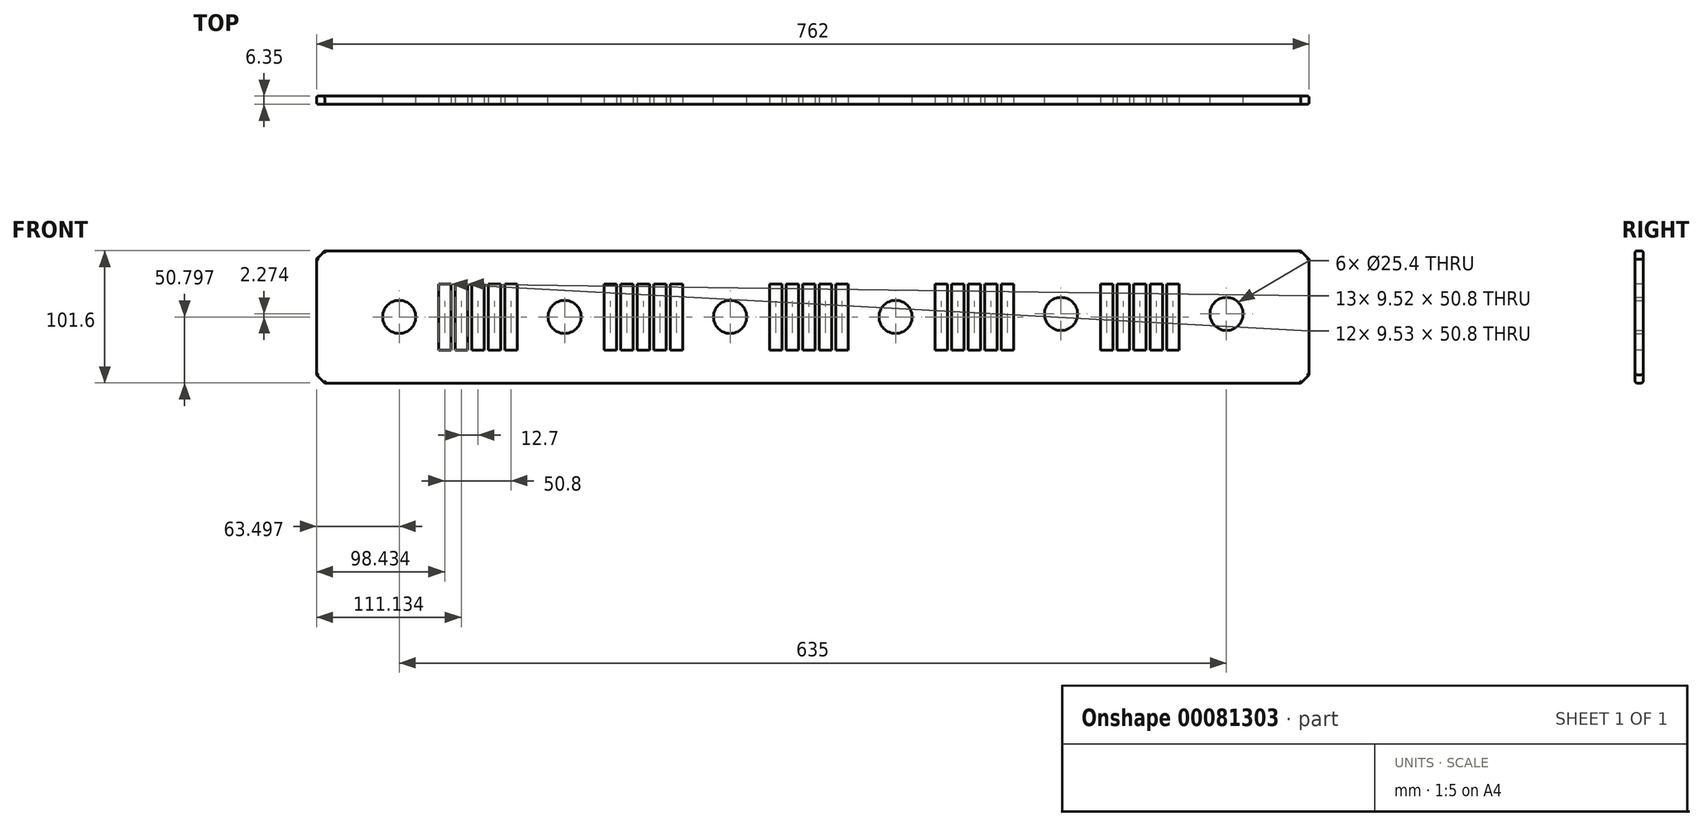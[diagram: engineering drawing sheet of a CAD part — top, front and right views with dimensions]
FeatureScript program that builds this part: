
annotation { "Feature Type Name" : "Feature", "Feature Type Description" : "" }
export const myFeature = defineFeature(function(context is Context, id is Id, definition is map)
    precondition{}
    {
        {
            var Q0;
            Q0=qCreatedBy(makeId("Front.planeOp"),FACE);
            var sketch = newSketch(context, id + "F0", { "sketchPlane" : qUnion([Q0])});
            skLineSegment(sketch, "E0.bottom", {"start": v(-162.42, 48.72) * mm, "end": v(599.58, 48.72) * mm});
            skLineSegment(sketch, "E0.top", {"start": v(-162.42, -52.88) * mm, "end": v(599.58, -52.88) * mm});
            skLineSegment(sketch, "E0.left", {"start": v(-162.42, 48.72) * mm, "end": v(-162.42, -52.88) * mm});
            skLineSegment(sketch, "E0.right", {"start": v(599.58, 48.72) * mm, "end": v(599.58, -52.88) * mm});
            skPoint(sketch, "E1.centerSnap0", {"position": v(-162.42, -2.08) * mm});
            skCircle(sketch, "E2", {"center": v(-98.92, -2.08) * mm, "radius": 12.7 * mm});
            skCircle(sketch, "E3", {"center": v(28.08, -2.08) * mm, "radius": 12.7 * mm});
            skCircle(sketch, "E4", {"center": v(155.08, -2.08) * mm, "radius": 12.7 * mm});
            skCircle(sketch, "E5", {"center": v(282.08, -2.08) * mm, "radius": 12.7 * mm});
            skCircle(sketch, "E6", {"center": v(409.08, 0.2) * mm, "radius": 12.7 * mm});
            skCircle(sketch, "E7", {"center": v(536.08, 0.2) * mm, "radius": 12.7 * mm});
            skSolve(sketch);
        }
        {
            var Q0;
            Q0=makeQuery(id+"F0.imprint","IMPRINT",FACE,{"disambiguationData":[TD([[makeQuery(id+"F0.imprint","IMPRINT",EDGE,{"derivedFrom":sQuery(id+"F0.wireOp",EDGE,"E0.bottom")}),-1.0]])]});
            var sketch = newSketch(context, id + "F1", { "sketchPlane" : qUnion([Q0])});
            skSolve(sketch);
        }
        {
            var Q0;
            Q0 = qSketchRegion(id + "F1", true);
            var Q1;
            Q1=makeQuery(id+"F0.imprint","IMPRINT",FACE,{"disambiguationData":[TD([[makeQuery(id+"F0.imprint","IMPRINT",EDGE,{"derivedFrom":sQuery(id+"F0.wireOp",EDGE,"E0.bottom")}),-1.0]])]});
            extrude(context, id + "F2", {"entities" : qUnion([Q0, Q1]), "depth" : 6.35 * mm});
        }
        {
            var Q0;
            Q0=makeQuery(id+"F2.opExtrude","SWEPT_EDGE",EDGE,{"disambiguationData":[OSD([sQuery(id+"F0.wireOp",EDGE,"E0.bottom"),sQuery(id+"F0.wireOp",EDGE,"E0.left")])]});
            var Q1;
            Q1=makeQuery(id+"F2.opExtrude","SWEPT_EDGE",EDGE,{"disambiguationData":[OSD([sQuery(id+"F0.wireOp",EDGE,"E0.top"),sQuery(id+"F0.wireOp",EDGE,"E0.left")])]});
            var Q2;
            Q2=makeQuery(id+"F2.opExtrude","SWEPT_EDGE",EDGE,{"disambiguationData":[OSD([sQuery(id+"F0.wireOp",EDGE,"E0.top"),sQuery(id+"F0.wireOp",EDGE,"E0.right")])]});
            var Q3;
            Q3=makeQuery(id+"F2.opExtrude","SWEPT_EDGE",EDGE,{"disambiguationData":[OSD([sQuery(id+"F0.wireOp",EDGE,"E0.bottom"),sQuery(id+"F0.wireOp",EDGE,"E0.right")])]});
            chamfer(context, id + "F3", {"entities" : qUnion([Q0, Q1, Q2, Q3]), "width" : 6.35 * mm, "tangentPropagation" : true});
        }
        {
            var Q0;
            Q0=makeQuery(id+"F2.opExtrude","CAP_FACE",FACE,{"disambiguationData":[OSD([sQuery(id+"F0.wireOp",EDGE,"E0.bottom"),sQuery(id+"F0.wireOp",EDGE,"E0.top"),sQuery(id+"F0.wireOp",EDGE,"E0.left"),sQuery(id+"F0.wireOp",EDGE,"E0.right"),sQuery(id+"F0.wireOp",EDGE,"E2"),sQuery(id+"F0.wireOp",EDGE,"E3"),sQuery(id+"F0.wireOp",EDGE,"E4"),sQuery(id+"F0.wireOp",EDGE,"E5"),sQuery(id+"F0.wireOp",EDGE,"E6"),sQuery(id+"F0.wireOp",EDGE,"E7")])],"isStart":false});
            var sketch = newSketch(context, id + "F4", { "sketchPlane" : qUnion([Q0])});
            skLineSegment(sketch, "E8.bottom", {"start": v(-68.75, -27.48) * mm, "end": v(-59.22, -27.48) * mm});
            skLineSegment(sketch, "E8.top", {"start": v(-68.75, 23.32) * mm, "end": v(-59.22, 23.32) * mm});
            skLineSegment(sketch, "E8.left", {"start": v(-68.75, -27.48) * mm, "end": v(-68.75, 23.32) * mm});
            skLineSegment(sketch, "E8.right", {"start": v(-59.22, -27.48) * mm, "end": v(-59.22, 23.32) * mm});
            skLineSegment(sketch, "E9.1.0.0", {"start": v(-46.52, -27.48) * mm, "end": v(-46.52, 23.32) * mm});
            skLineSegment(sketch, "E9.1.0.1", {"start": v(-56.05, -27.48) * mm, "end": v(-46.52, -27.48) * mm});
            skLineSegment(sketch, "E9.1.0.2", {"start": v(-56.05, 23.32) * mm, "end": v(-46.52, 23.32) * mm});
            skLineSegment(sketch, "E9.1.0.3", {"start": v(-56.05, -27.48) * mm, "end": v(-56.05, 23.32) * mm});
            skLineSegment(sketch, "E9.2.0.0", {"start": v(-33.82, -27.48) * mm, "end": v(-33.82, 23.32) * mm});
            skLineSegment(sketch, "E9.2.0.1", {"start": v(-43.35, -27.48) * mm, "end": v(-33.82, -27.48) * mm});
            skLineSegment(sketch, "E9.2.0.2", {"start": v(-43.35, 23.32) * mm, "end": v(-33.82, 23.32) * mm});
            skLineSegment(sketch, "E9.2.0.3", {"start": v(-43.35, -27.48) * mm, "end": v(-43.35, 23.32) * mm});
            skLineSegment(sketch, "E9.3.0.0", {"start": v(-21.12, -27.48) * mm, "end": v(-21.12, 23.32) * mm});
            skLineSegment(sketch, "E9.3.0.1", {"start": v(-30.65, -27.48) * mm, "end": v(-21.12, -27.48) * mm});
            skLineSegment(sketch, "E9.3.0.2", {"start": v(-30.65, 23.32) * mm, "end": v(-21.12, 23.32) * mm});
            skLineSegment(sketch, "E9.3.0.3", {"start": v(-30.65, -27.48) * mm, "end": v(-30.65, 23.32) * mm});
            skLineSegment(sketch, "E9.4.0.0", {"start": v(-8.42, -27.48) * mm, "end": v(-8.42, 23.32) * mm});
            skLineSegment(sketch, "E9.4.0.1", {"start": v(-17.95, -27.48) * mm, "end": v(-8.42, -27.48) * mm});
            skLineSegment(sketch, "E9.4.0.2", {"start": v(-17.95, 23.32) * mm, "end": v(-8.42, 23.32) * mm});
            skLineSegment(sketch, "E9.4.0.3", {"start": v(-17.95, -27.48) * mm, "end": v(-17.95, 23.32) * mm});
            skLineSegment(sketch, "E9.direction1", {"start": v(-59.22, -27.48) * mm, "end": v(-46.52, -27.48) * mm, "construction": true});
            skLineSegment(sketch, "E10.bottom", {"start": v(58.25, -27.48) * mm, "end": v(67.78, -27.48) * mm});
            skLineSegment(sketch, "E10.top", {"start": v(58.25, 23.32) * mm, "end": v(67.78, 23.32) * mm});
            skLineSegment(sketch, "E10.left", {"start": v(58.25, -27.48) * mm, "end": v(58.25, 23.32) * mm});
            skLineSegment(sketch, "E10.right", {"start": v(67.78, -27.48) * mm, "end": v(67.78, 23.32) * mm});
            skLineSegment(sketch, "E11.1.0.0", {"start": v(80.48, -27.48) * mm, "end": v(80.48, 23.32) * mm});
            skLineSegment(sketch, "E11.1.0.1", {"start": v(70.95, -27.48) * mm, "end": v(80.48, -27.48) * mm});
            skLineSegment(sketch, "E11.1.0.2", {"start": v(70.95, 23.32) * mm, "end": v(80.48, 23.32) * mm});
            skLineSegment(sketch, "E11.1.0.3", {"start": v(70.95, -27.48) * mm, "end": v(70.95, 23.32) * mm});
            skLineSegment(sketch, "E11.2.0.0", {"start": v(93.18, -27.48) * mm, "end": v(93.18, 23.32) * mm});
            skLineSegment(sketch, "E11.2.0.1", {"start": v(83.65, -27.48) * mm, "end": v(93.18, -27.48) * mm});
            skLineSegment(sketch, "E11.2.0.2", {"start": v(83.65, 23.32) * mm, "end": v(93.18, 23.32) * mm});
            skLineSegment(sketch, "E11.2.0.3", {"start": v(83.65, -27.48) * mm, "end": v(83.65, 23.32) * mm});
            skLineSegment(sketch, "E11.3.0.0", {"start": v(105.88, -27.48) * mm, "end": v(105.88, 23.32) * mm});
            skLineSegment(sketch, "E11.3.0.1", {"start": v(96.35, -27.48) * mm, "end": v(105.88, -27.48) * mm});
            skLineSegment(sketch, "E11.3.0.2", {"start": v(96.35, 23.32) * mm, "end": v(105.88, 23.32) * mm});
            skLineSegment(sketch, "E11.3.0.3", {"start": v(96.35, -27.48) * mm, "end": v(96.35, 23.32) * mm});
            skLineSegment(sketch, "E11.4.0.0", {"start": v(118.58, -27.48) * mm, "end": v(118.58, 23.32) * mm});
            skLineSegment(sketch, "E11.4.0.1", {"start": v(109.05, -27.48) * mm, "end": v(118.58, -27.48) * mm});
            skLineSegment(sketch, "E11.4.0.2", {"start": v(109.05, 23.32) * mm, "end": v(118.58, 23.32) * mm});
            skLineSegment(sketch, "E11.4.0.3", {"start": v(109.05, -27.48) * mm, "end": v(109.05, 23.32) * mm});
            skLineSegment(sketch, "E11.direction1", {"start": v(67.78, -27.48) * mm, "end": v(80.48, -27.48) * mm, "construction": true});
            skLineSegment(sketch, "E12.bottom", {"start": v(185.25, -27.48) * mm, "end": v(194.78, -27.48) * mm});
            skLineSegment(sketch, "E12.top", {"start": v(185.25, 23.32) * mm, "end": v(194.78, 23.32) * mm});
            skLineSegment(sketch, "E12.left", {"start": v(185.25, -27.48) * mm, "end": v(185.25, 23.32) * mm});
            skLineSegment(sketch, "E12.right", {"start": v(194.78, -27.48) * mm, "end": v(194.78, 23.32) * mm});
            skLineSegment(sketch, "E13.1.0.0", {"start": v(207.48, -27.48) * mm, "end": v(207.48, 23.32) * mm});
            skLineSegment(sketch, "E13.1.0.1", {"start": v(197.95, -27.48) * mm, "end": v(207.48, -27.48) * mm});
            skLineSegment(sketch, "E13.1.0.2", {"start": v(197.95, 23.32) * mm, "end": v(207.48, 23.32) * mm});
            skLineSegment(sketch, "E13.1.0.3", {"start": v(197.95, -27.48) * mm, "end": v(197.95, 23.32) * mm});
            skLineSegment(sketch, "E13.2.0.0", {"start": v(220.18, -27.48) * mm, "end": v(220.18, 23.32) * mm});
            skLineSegment(sketch, "E13.2.0.1", {"start": v(210.65, -27.48) * mm, "end": v(220.18, -27.48) * mm});
            skLineSegment(sketch, "E13.2.0.2", {"start": v(210.65, 23.32) * mm, "end": v(220.18, 23.32) * mm});
            skLineSegment(sketch, "E13.2.0.3", {"start": v(210.65, -27.48) * mm, "end": v(210.65, 23.32) * mm});
            skLineSegment(sketch, "E13.3.0.0", {"start": v(232.88, -27.48) * mm, "end": v(232.88, 23.32) * mm});
            skLineSegment(sketch, "E13.3.0.1", {"start": v(223.35, -27.48) * mm, "end": v(232.88, -27.48) * mm});
            skLineSegment(sketch, "E13.3.0.2", {"start": v(223.35, 23.32) * mm, "end": v(232.88, 23.32) * mm});
            skLineSegment(sketch, "E13.3.0.3", {"start": v(223.35, -27.48) * mm, "end": v(223.35, 23.32) * mm});
            skLineSegment(sketch, "E13.4.0.0", {"start": v(245.58, -27.48) * mm, "end": v(245.58, 23.32) * mm});
            skLineSegment(sketch, "E13.4.0.1", {"start": v(236.05, -27.48) * mm, "end": v(245.58, -27.48) * mm});
            skLineSegment(sketch, "E13.4.0.2", {"start": v(236.05, 23.32) * mm, "end": v(245.58, 23.32) * mm});
            skLineSegment(sketch, "E13.4.0.3", {"start": v(236.05, -27.48) * mm, "end": v(236.05, 23.32) * mm});
            skLineSegment(sketch, "E13.direction1", {"start": v(194.78, -27.48) * mm, "end": v(207.48, -27.48) * mm, "construction": true});
            skLineSegment(sketch, "E14.bottom", {"start": v(312.25, -27.48) * mm, "end": v(321.78, -27.48) * mm});
            skLineSegment(sketch, "E14.top", {"start": v(312.25, 23.32) * mm, "end": v(321.78, 23.32) * mm});
            skLineSegment(sketch, "E14.left", {"start": v(312.25, -27.48) * mm, "end": v(312.25, 23.32) * mm});
            skLineSegment(sketch, "E14.right", {"start": v(321.78, -27.48) * mm, "end": v(321.78, 23.32) * mm});
            skLineSegment(sketch, "E15.1.0.0", {"start": v(334.48, -27.48) * mm, "end": v(334.48, 23.32) * mm});
            skLineSegment(sketch, "E15.1.0.1", {"start": v(324.95, -27.48) * mm, "end": v(334.48, -27.48) * mm});
            skLineSegment(sketch, "E15.1.0.2", {"start": v(324.95, 23.32) * mm, "end": v(334.48, 23.32) * mm});
            skLineSegment(sketch, "E15.1.0.3", {"start": v(324.95, -27.48) * mm, "end": v(324.95, 23.32) * mm});
            skLineSegment(sketch, "E15.2.0.0", {"start": v(347.18, -27.48) * mm, "end": v(347.18, 23.32) * mm});
            skLineSegment(sketch, "E15.2.0.1", {"start": v(337.65, -27.48) * mm, "end": v(347.18, -27.48) * mm});
            skLineSegment(sketch, "E15.2.0.2", {"start": v(337.65, 23.32) * mm, "end": v(347.18, 23.32) * mm});
            skLineSegment(sketch, "E15.2.0.3", {"start": v(337.65, -27.48) * mm, "end": v(337.65, 23.32) * mm});
            skLineSegment(sketch, "E15.3.0.0", {"start": v(359.88, -27.48) * mm, "end": v(359.88, 23.32) * mm});
            skLineSegment(sketch, "E15.3.0.1", {"start": v(350.35, -27.48) * mm, "end": v(359.88, -27.48) * mm});
            skLineSegment(sketch, "E15.3.0.2", {"start": v(350.35, 23.32) * mm, "end": v(359.88, 23.32) * mm});
            skLineSegment(sketch, "E15.3.0.3", {"start": v(350.35, -27.48) * mm, "end": v(350.35, 23.32) * mm});
            skLineSegment(sketch, "E15.4.0.0", {"start": v(372.58, -27.48) * mm, "end": v(372.58, 23.32) * mm});
            skLineSegment(sketch, "E15.4.0.1", {"start": v(363.05, -27.48) * mm, "end": v(372.58, -27.48) * mm});
            skLineSegment(sketch, "E15.4.0.2", {"start": v(363.05, 23.32) * mm, "end": v(372.58, 23.32) * mm});
            skLineSegment(sketch, "E15.4.0.3", {"start": v(363.05, -27.48) * mm, "end": v(363.05, 23.32) * mm});
            skLineSegment(sketch, "E15.direction1", {"start": v(321.78, -27.48) * mm, "end": v(334.48, -27.48) * mm, "construction": true});
            skLineSegment(sketch, "E16.bottom", {"start": v(439.25, -27.48) * mm, "end": v(448.78, -27.48) * mm});
            skLineSegment(sketch, "E16.top", {"start": v(439.25, 23.32) * mm, "end": v(448.78, 23.32) * mm});
            skLineSegment(sketch, "E16.left", {"start": v(439.25, -27.48) * mm, "end": v(439.25, 23.32) * mm});
            skLineSegment(sketch, "E16.right", {"start": v(448.78, -27.48) * mm, "end": v(448.78, 23.32) * mm});
            skLineSegment(sketch, "E17.1.0.0", {"start": v(461.48, -27.48) * mm, "end": v(461.48, 23.32) * mm});
            skLineSegment(sketch, "E17.1.0.1", {"start": v(451.95, -27.48) * mm, "end": v(461.48, -27.48) * mm});
            skLineSegment(sketch, "E17.1.0.2", {"start": v(451.95, 23.32) * mm, "end": v(461.48, 23.32) * mm});
            skLineSegment(sketch, "E17.1.0.3", {"start": v(451.95, -27.48) * mm, "end": v(451.95, 23.32) * mm});
            skLineSegment(sketch, "E17.2.0.0", {"start": v(474.18, -27.48) * mm, "end": v(474.18, 23.32) * mm});
            skLineSegment(sketch, "E17.2.0.1", {"start": v(464.65, -27.48) * mm, "end": v(474.18, -27.48) * mm});
            skLineSegment(sketch, "E17.2.0.2", {"start": v(464.65, 23.32) * mm, "end": v(474.18, 23.32) * mm});
            skLineSegment(sketch, "E17.2.0.3", {"start": v(464.65, -27.48) * mm, "end": v(464.65, 23.32) * mm});
            skLineSegment(sketch, "E17.3.0.0", {"start": v(486.88, -27.48) * mm, "end": v(486.88, 23.32) * mm});
            skLineSegment(sketch, "E17.3.0.1", {"start": v(477.35, -27.48) * mm, "end": v(486.88, -27.48) * mm});
            skLineSegment(sketch, "E17.3.0.2", {"start": v(477.35, 23.32) * mm, "end": v(486.88, 23.32) * mm});
            skLineSegment(sketch, "E17.3.0.3", {"start": v(477.35, -27.48) * mm, "end": v(477.35, 23.32) * mm});
            skLineSegment(sketch, "E17.4.0.0", {"start": v(499.58, -27.48) * mm, "end": v(499.58, 23.32) * mm});
            skLineSegment(sketch, "E17.4.0.1", {"start": v(490.05, -27.48) * mm, "end": v(499.58, -27.48) * mm});
            skLineSegment(sketch, "E17.4.0.2", {"start": v(490.05, 23.32) * mm, "end": v(499.58, 23.32) * mm});
            skLineSegment(sketch, "E17.4.0.3", {"start": v(490.05, -27.48) * mm, "end": v(490.05, 23.32) * mm});
            skLineSegment(sketch, "E17.direction1", {"start": v(448.78, -27.48) * mm, "end": v(461.48, -27.48) * mm, "construction": true});
            skSolve(sketch);
        }
        {
            var Q0;
            Q0 = qSketchRegion(id + "F4", true);
            extrude(context, id + "F5", {"entities" : qUnion([Q0]), "operationType" : NewBodyOperationType.REMOVE, "endBound" : BoundingType.THROUGH_ALL, "oppositeDirection" : true, "depth" : 25.4 * mm});
        }
        {
            var Q0;
            Q0=makeQuery(id+"F2.opExtrude","CAP_EDGE",EDGE,{"disambiguationData":[OSD([sQuery(id+"F0.wireOp",EDGE,"E0.bottom")])],"isStart":false});
            var Q1;
            Q1=makeQuery(id+"F2.opExtrude","CAP_EDGE",EDGE,{"disambiguationData":[OSD([sQuery(id+"F0.wireOp",EDGE,"E0.left")])],"isStart":true});
            var Q2;
            {var subQ0=sQuery(id+"F0.wireOp",EDGE,"E0.left");var subQ1=sQuery(id+"F0.wireOp",EDGE,"E0.bottom");Q2=makeQuery(id+"F3.opChamfer","BLEND_EDGE",EDGE,{"blendedFrom":[makeQuery(id+"F2.opExtrude","SWEPT_EDGE",EDGE,{"disambiguationData":[OSD([subQ1,subQ0])]}),makeQuery(id+"F2.opExtrude","CAP_FACE",FACE,{"disambiguationData":[OSD([subQ1,sQuery(id+"F0.wireOp",EDGE,"E0.top"),subQ0,sQuery(id+"F0.wireOp",EDGE,"E0.right"),sQuery(id+"F0.wireOp",EDGE,"E2"),sQuery(id+"F0.wireOp",EDGE,"E3"),sQuery(id+"F0.wireOp",EDGE,"E4"),sQuery(id+"F0.wireOp",EDGE,"E5"),sQuery(id+"F0.wireOp",EDGE,"E6"),sQuery(id+"F0.wireOp",EDGE,"E7")])],"isStart":false})],"blendedInto":[makeQuery(id+"F2.opExtrude","CAP_FACE",FACE,{"disambiguationData":[OSD([subQ1,sQuery(id+"F0.wireOp",EDGE,"E0.top"),subQ0,sQuery(id+"F0.wireOp",EDGE,"E0.right"),sQuery(id+"F0.wireOp",EDGE,"E2"),sQuery(id+"F0.wireOp",EDGE,"E3"),sQuery(id+"F0.wireOp",EDGE,"E4"),sQuery(id+"F0.wireOp",EDGE,"E5"),sQuery(id+"F0.wireOp",EDGE,"E6"),sQuery(id+"F0.wireOp",EDGE,"E7")])],"isStart":false})]});}
            var Q3;
            Q3=makeQuery(id+"F2.opExtrude","CAP_EDGE",EDGE,{"disambiguationData":[OSD([sQuery(id+"F0.wireOp",EDGE,"E0.left")])],"isStart":false});
            var Q4;
            {var subQ0=sQuery(id+"F0.wireOp",EDGE,"E0.left");var subQ1=sQuery(id+"F0.wireOp",EDGE,"E0.top");Q4=makeQuery(id+"F3.opChamfer","BLEND_EDGE",EDGE,{"blendedFrom":[makeQuery(id+"F2.opExtrude","SWEPT_EDGE",EDGE,{"disambiguationData":[OSD([subQ1,subQ0])]}),makeQuery(id+"F2.opExtrude","CAP_FACE",FACE,{"disambiguationData":[OSD([sQuery(id+"F0.wireOp",EDGE,"E0.bottom"),subQ1,subQ0,sQuery(id+"F0.wireOp",EDGE,"E0.right"),sQuery(id+"F0.wireOp",EDGE,"E2"),sQuery(id+"F0.wireOp",EDGE,"E3"),sQuery(id+"F0.wireOp",EDGE,"E4"),sQuery(id+"F0.wireOp",EDGE,"E5"),sQuery(id+"F0.wireOp",EDGE,"E6"),sQuery(id+"F0.wireOp",EDGE,"E7")])],"isStart":false})],"blendedInto":[makeQuery(id+"F2.opExtrude","CAP_FACE",FACE,{"disambiguationData":[OSD([sQuery(id+"F0.wireOp",EDGE,"E0.bottom"),subQ1,subQ0,sQuery(id+"F0.wireOp",EDGE,"E0.right"),sQuery(id+"F0.wireOp",EDGE,"E2"),sQuery(id+"F0.wireOp",EDGE,"E3"),sQuery(id+"F0.wireOp",EDGE,"E4"),sQuery(id+"F0.wireOp",EDGE,"E5"),sQuery(id+"F0.wireOp",EDGE,"E6"),sQuery(id+"F0.wireOp",EDGE,"E7")])],"isStart":false})]});}
            var Q5;
            Q5=makeQuery(id+"F2.opExtrude","CAP_EDGE",EDGE,{"disambiguationData":[OSD([sQuery(id+"F0.wireOp",EDGE,"E0.top")])],"isStart":false});
            var Q6;
            {var subQ0=sQuery(id+"F0.wireOp",EDGE,"E0.right");var subQ1=sQuery(id+"F0.wireOp",EDGE,"E0.top");Q6=makeQuery(id+"F3.opChamfer","BLEND_EDGE",EDGE,{"blendedFrom":[makeQuery(id+"F2.opExtrude","SWEPT_EDGE",EDGE,{"disambiguationData":[OSD([subQ1,subQ0])]}),makeQuery(id+"F2.opExtrude","CAP_FACE",FACE,{"disambiguationData":[OSD([sQuery(id+"F0.wireOp",EDGE,"E0.bottom"),subQ1,sQuery(id+"F0.wireOp",EDGE,"E0.left"),subQ0,sQuery(id+"F0.wireOp",EDGE,"E2"),sQuery(id+"F0.wireOp",EDGE,"E3"),sQuery(id+"F0.wireOp",EDGE,"E4"),sQuery(id+"F0.wireOp",EDGE,"E5"),sQuery(id+"F0.wireOp",EDGE,"E6"),sQuery(id+"F0.wireOp",EDGE,"E7")])],"isStart":false})],"blendedInto":[makeQuery(id+"F2.opExtrude","CAP_FACE",FACE,{"disambiguationData":[OSD([sQuery(id+"F0.wireOp",EDGE,"E0.bottom"),subQ1,sQuery(id+"F0.wireOp",EDGE,"E0.left"),subQ0,sQuery(id+"F0.wireOp",EDGE,"E2"),sQuery(id+"F0.wireOp",EDGE,"E3"),sQuery(id+"F0.wireOp",EDGE,"E4"),sQuery(id+"F0.wireOp",EDGE,"E5"),sQuery(id+"F0.wireOp",EDGE,"E6"),sQuery(id+"F0.wireOp",EDGE,"E7")])],"isStart":false})]});}
            var Q7;
            Q7=makeQuery(id+"F2.opExtrude","CAP_EDGE",EDGE,{"disambiguationData":[OSD([sQuery(id+"F0.wireOp",EDGE,"E0.right")])],"isStart":false});
            var Q8;
            {var subQ0=sQuery(id+"F0.wireOp",EDGE,"E0.right");var subQ1=sQuery(id+"F0.wireOp",EDGE,"E0.bottom");Q8=makeQuery(id+"F3.opChamfer","BLEND_EDGE",EDGE,{"blendedFrom":[makeQuery(id+"F2.opExtrude","SWEPT_EDGE",EDGE,{"disambiguationData":[OSD([subQ1,subQ0])]}),makeQuery(id+"F2.opExtrude","CAP_FACE",FACE,{"disambiguationData":[OSD([subQ1,sQuery(id+"F0.wireOp",EDGE,"E0.top"),sQuery(id+"F0.wireOp",EDGE,"E0.left"),subQ0,sQuery(id+"F0.wireOp",EDGE,"E2"),sQuery(id+"F0.wireOp",EDGE,"E3"),sQuery(id+"F0.wireOp",EDGE,"E4"),sQuery(id+"F0.wireOp",EDGE,"E5"),sQuery(id+"F0.wireOp",EDGE,"E6"),sQuery(id+"F0.wireOp",EDGE,"E7")])],"isStart":false})],"blendedInto":[makeQuery(id+"F2.opExtrude","CAP_FACE",FACE,{"disambiguationData":[OSD([subQ1,sQuery(id+"F0.wireOp",EDGE,"E0.top"),sQuery(id+"F0.wireOp",EDGE,"E0.left"),subQ0,sQuery(id+"F0.wireOp",EDGE,"E2"),sQuery(id+"F0.wireOp",EDGE,"E3"),sQuery(id+"F0.wireOp",EDGE,"E4"),sQuery(id+"F0.wireOp",EDGE,"E5"),sQuery(id+"F0.wireOp",EDGE,"E6"),sQuery(id+"F0.wireOp",EDGE,"E7")])],"isStart":false})]});}
            var Q9;
            {var subQ0=sQuery(id+"F0.wireOp",EDGE,"E0.right");var subQ1=sQuery(id+"F0.wireOp",EDGE,"E0.bottom");Q9=makeQuery(id+"F3.opChamfer","BLEND_EDGE",EDGE,{"blendedFrom":[makeQuery(id+"F2.opExtrude","SWEPT_EDGE",EDGE,{"disambiguationData":[OSD([subQ1,subQ0])]}),makeQuery(id+"F2.opExtrude","CAP_FACE",FACE,{"disambiguationData":[OSD([subQ1,sQuery(id+"F0.wireOp",EDGE,"E0.top"),sQuery(id+"F0.wireOp",EDGE,"E0.left"),subQ0,sQuery(id+"F0.wireOp",EDGE,"E2"),sQuery(id+"F0.wireOp",EDGE,"E3"),sQuery(id+"F0.wireOp",EDGE,"E4"),sQuery(id+"F0.wireOp",EDGE,"E5"),sQuery(id+"F0.wireOp",EDGE,"E6"),sQuery(id+"F0.wireOp",EDGE,"E7")])],"isStart":true})],"blendedInto":[makeQuery(id+"F2.opExtrude","CAP_FACE",FACE,{"disambiguationData":[OSD([subQ1,sQuery(id+"F0.wireOp",EDGE,"E0.top"),sQuery(id+"F0.wireOp",EDGE,"E0.left"),subQ0,sQuery(id+"F0.wireOp",EDGE,"E2"),sQuery(id+"F0.wireOp",EDGE,"E3"),sQuery(id+"F0.wireOp",EDGE,"E4"),sQuery(id+"F0.wireOp",EDGE,"E5"),sQuery(id+"F0.wireOp",EDGE,"E6"),sQuery(id+"F0.wireOp",EDGE,"E7")])],"isStart":true})]});}
            var Q10;
            Q10=makeQuery(id+"F2.opExtrude","CAP_EDGE",EDGE,{"disambiguationData":[OSD([sQuery(id+"F0.wireOp",EDGE,"E0.bottom")])],"isStart":true});
            var Q11;
            Q11=makeQuery(id+"F2.opExtrude","CAP_EDGE",EDGE,{"disambiguationData":[OSD([sQuery(id+"F0.wireOp",EDGE,"E0.right")])],"isStart":true});
            var Q12;
            {var subQ0=sQuery(id+"F0.wireOp",EDGE,"E0.right");var subQ1=sQuery(id+"F0.wireOp",EDGE,"E0.top");Q12=makeQuery(id+"F3.opChamfer","BLEND_EDGE",EDGE,{"blendedFrom":[makeQuery(id+"F2.opExtrude","SWEPT_EDGE",EDGE,{"disambiguationData":[OSD([subQ1,subQ0])]}),makeQuery(id+"F2.opExtrude","CAP_FACE",FACE,{"disambiguationData":[OSD([sQuery(id+"F0.wireOp",EDGE,"E0.bottom"),subQ1,sQuery(id+"F0.wireOp",EDGE,"E0.left"),subQ0,sQuery(id+"F0.wireOp",EDGE,"E2"),sQuery(id+"F0.wireOp",EDGE,"E3"),sQuery(id+"F0.wireOp",EDGE,"E4"),sQuery(id+"F0.wireOp",EDGE,"E5"),sQuery(id+"F0.wireOp",EDGE,"E6"),sQuery(id+"F0.wireOp",EDGE,"E7")])],"isStart":true})],"blendedInto":[makeQuery(id+"F2.opExtrude","CAP_FACE",FACE,{"disambiguationData":[OSD([sQuery(id+"F0.wireOp",EDGE,"E0.bottom"),subQ1,sQuery(id+"F0.wireOp",EDGE,"E0.left"),subQ0,sQuery(id+"F0.wireOp",EDGE,"E2"),sQuery(id+"F0.wireOp",EDGE,"E3"),sQuery(id+"F0.wireOp",EDGE,"E4"),sQuery(id+"F0.wireOp",EDGE,"E5"),sQuery(id+"F0.wireOp",EDGE,"E6"),sQuery(id+"F0.wireOp",EDGE,"E7")])],"isStart":true})]});}
            var Q13;
            Q13=makeQuery(id+"F2.opExtrude","CAP_EDGE",EDGE,{"disambiguationData":[OSD([sQuery(id+"F0.wireOp",EDGE,"E0.top")])],"isStart":true});
            var Q14;
            {var subQ0=sQuery(id+"F0.wireOp",EDGE,"E0.left");var subQ1=sQuery(id+"F0.wireOp",EDGE,"E0.top");Q14=makeQuery(id+"F3.opChamfer","BLEND_EDGE",EDGE,{"blendedFrom":[makeQuery(id+"F2.opExtrude","SWEPT_EDGE",EDGE,{"disambiguationData":[OSD([subQ1,subQ0])]}),makeQuery(id+"F2.opExtrude","CAP_FACE",FACE,{"disambiguationData":[OSD([sQuery(id+"F0.wireOp",EDGE,"E0.bottom"),subQ1,subQ0,sQuery(id+"F0.wireOp",EDGE,"E0.right"),sQuery(id+"F0.wireOp",EDGE,"E2"),sQuery(id+"F0.wireOp",EDGE,"E3"),sQuery(id+"F0.wireOp",EDGE,"E4"),sQuery(id+"F0.wireOp",EDGE,"E5"),sQuery(id+"F0.wireOp",EDGE,"E6"),sQuery(id+"F0.wireOp",EDGE,"E7")])],"isStart":true})],"blendedInto":[makeQuery(id+"F2.opExtrude","CAP_FACE",FACE,{"disambiguationData":[OSD([sQuery(id+"F0.wireOp",EDGE,"E0.bottom"),subQ1,subQ0,sQuery(id+"F0.wireOp",EDGE,"E0.right"),sQuery(id+"F0.wireOp",EDGE,"E2"),sQuery(id+"F0.wireOp",EDGE,"E3"),sQuery(id+"F0.wireOp",EDGE,"E4"),sQuery(id+"F0.wireOp",EDGE,"E5"),sQuery(id+"F0.wireOp",EDGE,"E6"),sQuery(id+"F0.wireOp",EDGE,"E7")])],"isStart":true})]});}
            fillet(context, id + "F6", {"entities" : qUnion([Q0, Q1, Q2, Q3, Q4, Q5, Q6, Q7, Q8, Q9, Q10, Q11, Q12, Q13, Q14]), "radius" : 1.6 * mm, "tangentPropagation" : true, "allowEdgeOverflow" : false});
        }
    });
